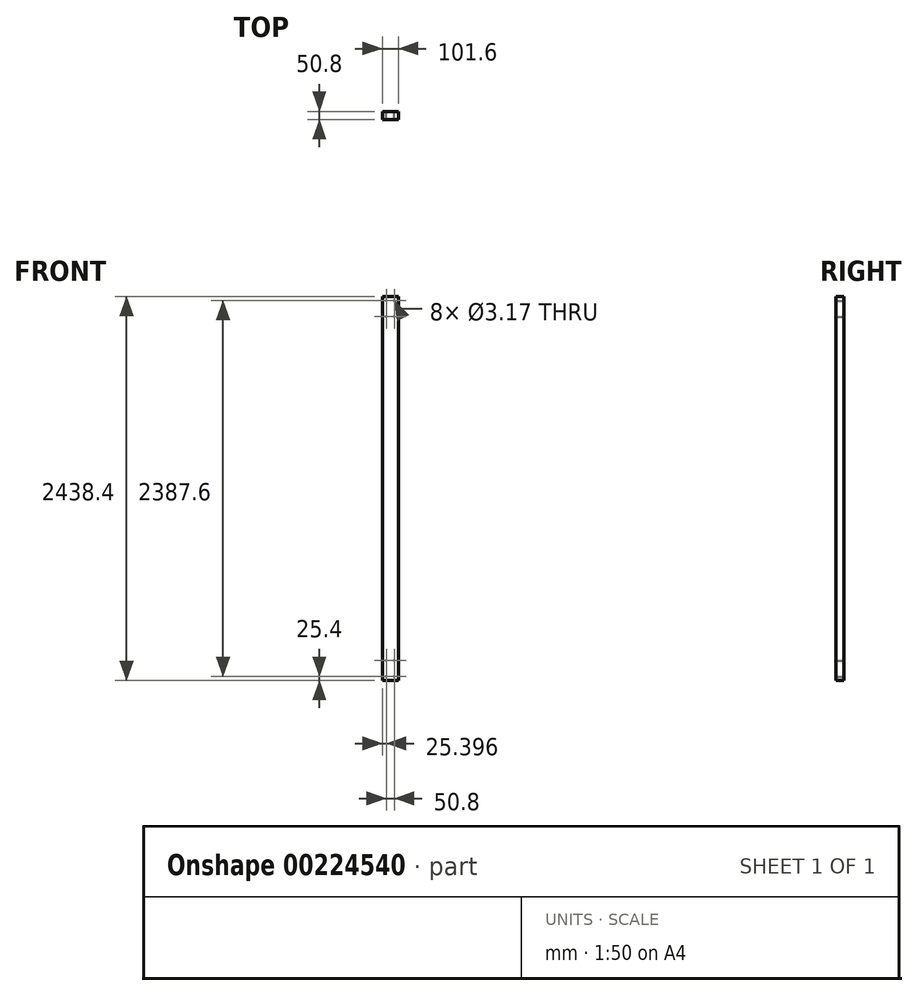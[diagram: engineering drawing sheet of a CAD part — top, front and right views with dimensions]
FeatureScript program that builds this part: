
annotation { "Feature Type Name" : "Feature", "Feature Type Description" : "" }
export const myFeature = defineFeature(function(context is Context, id is Id, definition is map)
    precondition{}
    {
        {
            var Q0;
            Q0=qCreatedBy(makeId("Front.planeOp"),FACE);
            var sketch = newSketch(context, id + "F0", { "sketchPlane" : qUnion([Q0])});
            skLineSegment(sketch, "E0.bottom", {"start": v(-42, 2311.4) * mm, "end": v(59.6, 2311.4) * mm});
            skLineSegment(sketch, "E0.top", {"start": v(-42, -127) * mm, "end": v(59.6, -127) * mm});
            skLineSegment(sketch, "E0.left", {"start": v(-42, 2311.4) * mm, "end": v(-42, -127) * mm});
            skLineSegment(sketch, "E0.right", {"start": v(59.6, 2311.4) * mm, "end": v(59.6, -127) * mm});
            skCircle(sketch, "E1", {"center": v(-16.6, 2286) * mm, "radius": 1.59 * mm});
            skCircle(sketch, "E2", {"center": v(34.2, 2286) * mm, "radius": 1.59 * mm});
            skCircle(sketch, "E3", {"center": v(-16.6, 2184.4) * mm, "radius": 1.59 * mm});
            skCircle(sketch, "E4", {"center": v(34.2, 2184.4) * mm, "radius": 1.59 * mm});
            skCircle(sketch, "E5", {"center": v(-16.6, -101.6) * mm, "radius": 1.59 * mm});
            skCircle(sketch, "E6", {"center": v(34.2, -101.6) * mm, "radius": 1.59 * mm});
            skCircle(sketch, "E7", {"center": v(-16.6, 0) * mm, "radius": 1.59 * mm});
            skCircle(sketch, "E8", {"center": v(34.2, 0) * mm, "radius": 1.59 * mm});
            skSolve(sketch);
        }
        {
            var Q0;
            Q0=makeQuery(id+"F0.imprint","IMPRINT",FACE,{"disambiguationData":[TD([[makeQuery(id+"F0.imprint","IMPRINT",EDGE,{"derivedFrom":sQuery(id+"F0.wireOp",EDGE,"E0.bottom")}),-1.0]])]});
            extrude(context, id + "F1", {"entities" : qUnion([Q0]), "depth" : 50.8 * mm});
        }
    });
